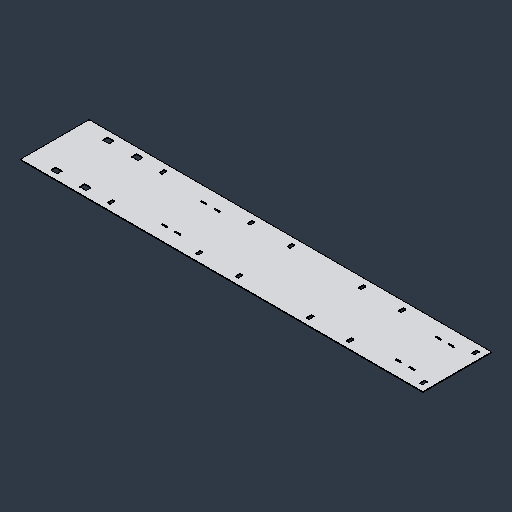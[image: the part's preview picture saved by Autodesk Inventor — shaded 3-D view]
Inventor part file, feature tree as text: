
AUTODESK INVENTOR PART (.ipt)
format: ipt  version: 2024.3 (Build 283343000, 343)  size: 196,608 bytes
history: native  units: mm (DEFAULTED — no unit token found)
features: mirror x1
ambient origin geometry x8: Origin, YZ Plane, XZ Plane, XY Plane, X Axis, Y Axis, Z Axis, Center Point
bodies: Solid1 (feature_tree)
feature tree (1):
  mirror  "Mirror1"
